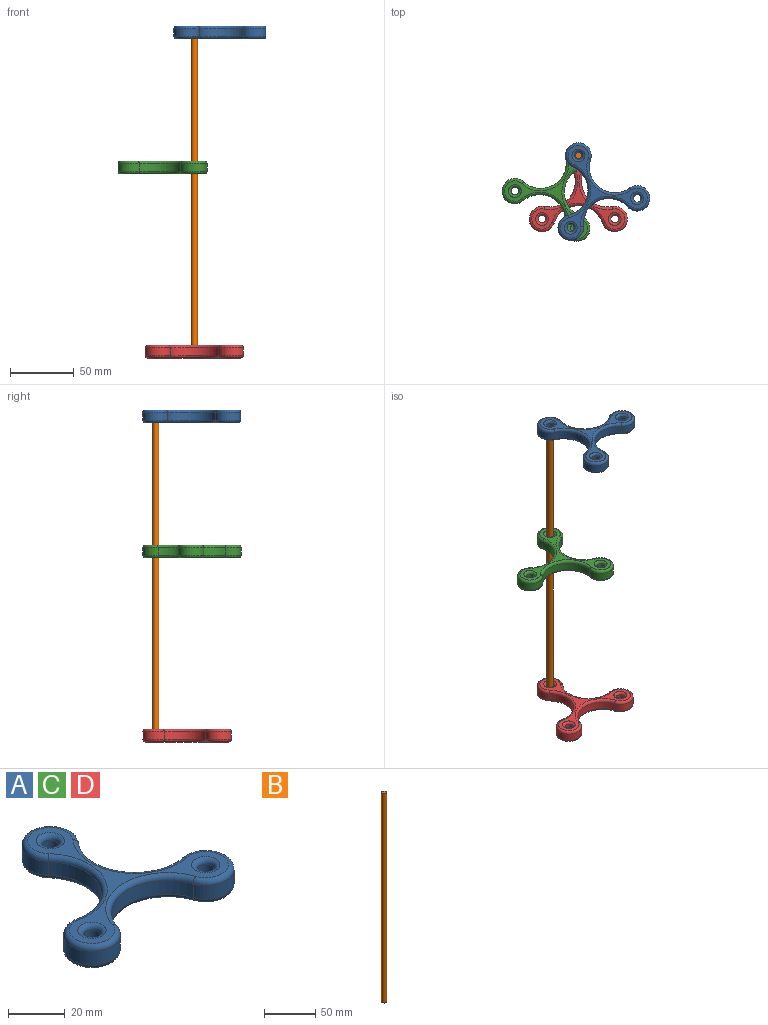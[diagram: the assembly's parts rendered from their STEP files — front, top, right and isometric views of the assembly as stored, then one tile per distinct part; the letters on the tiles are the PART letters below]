
ASSEMBLY  parts=4 mates=3
PART A: 29 faces, bbox 78.6x70.9x10 mm
  f0: cylinder r=20mm len=37.94mm, axis (0,0,-1), area 299.5mm2, adj f1,f5,f15,f24
  f1: cylinder r=10mm len=20mm, axis (0,0,-1), area 275.4mm2, adj f0,f2,f14,f23
  f2: cylinder r=20mm len=33.25mm, axis (0,0,-1), area 299.5mm2, adj f1,f3,f16,f25
  f3: cylinder r=10mm len=20mm, axis (0,0,-1), area 275.4mm2, adj f2,f4,f18,f27
  f4: cylinder r=20mm len=33.25mm, axis (0,0,-1), area 299.5mm2, adj f3,f5,f19,f28
  f5: cylinder r=10mm len=20mm, axis (0,0,-1), area 275.4mm2, adj f0,f4,f17,f26
  f6: plane 72.9x65.28mm, normal (0,0,1), area 607.1mm2, adj f11,f12,f13,f14,f15,f16,f17,f18
  f7: plane 72.9x65.28mm, normal (0,0,-1), area 607.1mm2, adj f20,f21,f22,f23,f24,f25,f26,f27
  f8: cylinder r=3mm len=6mm, axis (0,0,-1), area 113.1mm2, adj f13,f20
  f9: cylinder r=3mm len=6mm, axis (0,0,-1), area 113.1mm2, adj f12,f21
  f10: cylinder r=3mm len=6mm, axis (0,0,-1), area 113.1mm2, adj f11,f22
  f11: torus R=5mm, axis (0,0,1), area 73.6mm2, adj f6,f10
  f12: torus R=5mm, axis (0,0,1), area 73.6mm2, adj f6,f9
  f13: torus R=5mm, axis (0,0,1), area 73.6mm2, adj f6,f8
  f14: torus R=8mm, axis (0,0,1), area 133.7mm2, adj f1,f6,f15,f16
  f15: torus R=22mm, axis (0,0,1), area 162.5mm2, adj f0,f6,f14,f17
  f16: torus R=22mm, axis (0,0,1), area 162.5mm2, adj f2,f6,f14,f18
  f17: torus R=8mm, axis (0,0,1), area 133.7mm2, adj f5,f6,f15,f19
  f18: torus R=8mm, axis (0,0,1), area 133.7mm2, adj f3,f6,f16,f19
  f19: torus R=22mm, axis (0,0,1), area 162.5mm2, adj f4,f6,f17,f18
  f20: torus R=5mm, axis (0,0,1), area 73.6mm2, adj f7,f8
  f21: torus R=5mm, axis (0,0,1), area 73.6mm2, adj f7,f9
  f22: torus R=5mm, axis (0,0,1), area 73.6mm2, adj f7,f10
  f23: torus R=8mm, axis (0,0,1), area 133.7mm2, adj f1,f7,f24,f25
  f24: torus R=22mm, axis (0,0,1), area 162.5mm2, adj f0,f7,f23,f26
  f25: torus R=22mm, axis (0,0,1), area 162.5mm2, adj f2,f7,f23,f27
  f26: torus R=8mm, axis (0,0,1), area 133.7mm2, adj f5,f7,f24,f28
  f27: torus R=8mm, axis (0,0,1), area 133.7mm2, adj f3,f7,f25,f28
  f28: torus R=22mm, axis (0,0,1), area 162.5mm2, adj f4,f7,f26,f27
PART B: 3 faces, bbox 5x5x250 mm
  f0: cylinder r=2.5mm len=250mm, axis (0,0,-1), area 3927mm2, adj f1,f2
  f1: plane 5x5mm, normal (0,0,1), area 19.6mm2, adj f0
  f2: plane 5x5mm, normal (0,0,-1), area 19.6mm2, adj f0
PART C: same geometry as A
PART D: same geometry as A
PLACE A rot(axis=(0,0,1),24deg) t=(42.53,16.72,114.59)mm
PLACE B t=(29.19,46.74,-130.41)mm fixed
PLACE C rot(axis=(0,0,-1),150.9deg) t=(12.31,18.56,8.76)mm
PLACE D t=(29.19,13.89,-135.41)mm
MATE revolute D.f3 <-> B.f0  axis (0,0,-1) through (29.19,46.74,-130.41)mm
MATE cylindrical B.f0 <-> C.f5  axis (0,0,-1) through (29.19,46.74,-5.41)mm
MATE revolute B.f0 <-> A.f3  axis (0,0,-1) through (29.19,46.74,119.59)mm
